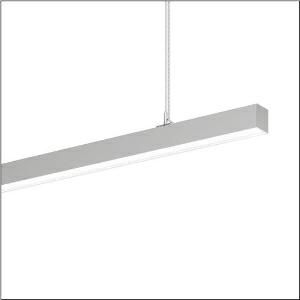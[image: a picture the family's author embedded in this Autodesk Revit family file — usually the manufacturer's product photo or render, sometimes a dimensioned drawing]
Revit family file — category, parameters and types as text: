
# Revit family: silica_r__21_51mx33da47sb_3209
name_source: partatom
category: Lighting Fixtures
units: mm (PartAtom-declared; Revit-internal decimal feet)

## family parameters
Cut with Voids When Loaded = No
Host = Face
Light Source = No
Part Type = Normal
Room Calculation Point = No
Round Connector Dimension = Use Diameter
Shared = No

## types (1)
- --- (1 x LED, 5910 lm, 38.4 W, 4000K)
    Apparent Load = 38 VA
    CIE Flux Codes = 78 96 99 55 100
    Color Rendering = 80
    Color Temperature = 4000K
    Default Elevation = 1800 mm
    Description = Silica® 21, office luminaire, primary optical cover: prismatic diffuser, of PMMA, CAT 2 (L<= 3000cd/m²), light emission: direct/indirect distribution, primary light characteristic: symmetric, installation type: suspended mounting, LED, rated luminous flux: 5.910lm, luminous efficacy: 154lm/W, light colour: 840, colour temperature: 4000K, with terminal, 3+2-pole, max. 2.5mm², mains connection: 220..240V, AC, 50/60Hz, rated input power: 38.4W, luminaire housing, of aluminium, metallic grey (RAL 9006), length: 1.204mm, width: 53mm, height: 53mm, protection rating (complete): IP20, insulation class (complete): insulation class I (protective earthing), certification: CE, permissible operating ambient temperature: 0..+35°C, standard: EN 50419, packaging unit: 1 piece
    Height = 53 mm
    Lamp = 1 x LED
    Lamp Light Flux = 5910 lm
    Lamp Power = 38.4 W
    Lamp count = 1
    Length = 1204 mm
    Luminous efficacy = 154 lm/W
    Manufacturer = Siteco
    ModVariant = No
    Model = 51MX33DA47SB
    Mounting Place = Ceiling
    Mounting Type = Pendant
    Number of Poles = 1
    OnlyDefault = Yes
    Power Factor = 1
    Product Name = Silica® 21
    Product group = office luminaire | ceiling pendant
    ProductGroupID = 902
    Protection Class = Protection class I
    Protection Degree = IP 20
    RLX_Detail_Level = 1
    RLX_Emergency_Light_Flux = 0 lm
    RLX_Emergency_Type = 0
    RLX_Emergency_Type_DB = No
    RlxData = <blob elided: 23173 chars, md5=3772c766>
    Socket = socket
    Standby Power = 0 W
    System Light Flux = 5910 lm
    System Power = 38 W
    Type Comments = factory setting: luminous flux: 100 % | dim-lin: 254 | 323 mA
    Type Image = l_1335864.jpg
    URL = http://relux.com
    VarID = @adj_087755
    Voltage = 0 V
    Weight = 0.00 kg
    Width = 53 mm

## geometry (parser evidence)
native form markers: Blend x4, Sweep x14
no freeform markers — native parametric forms only
